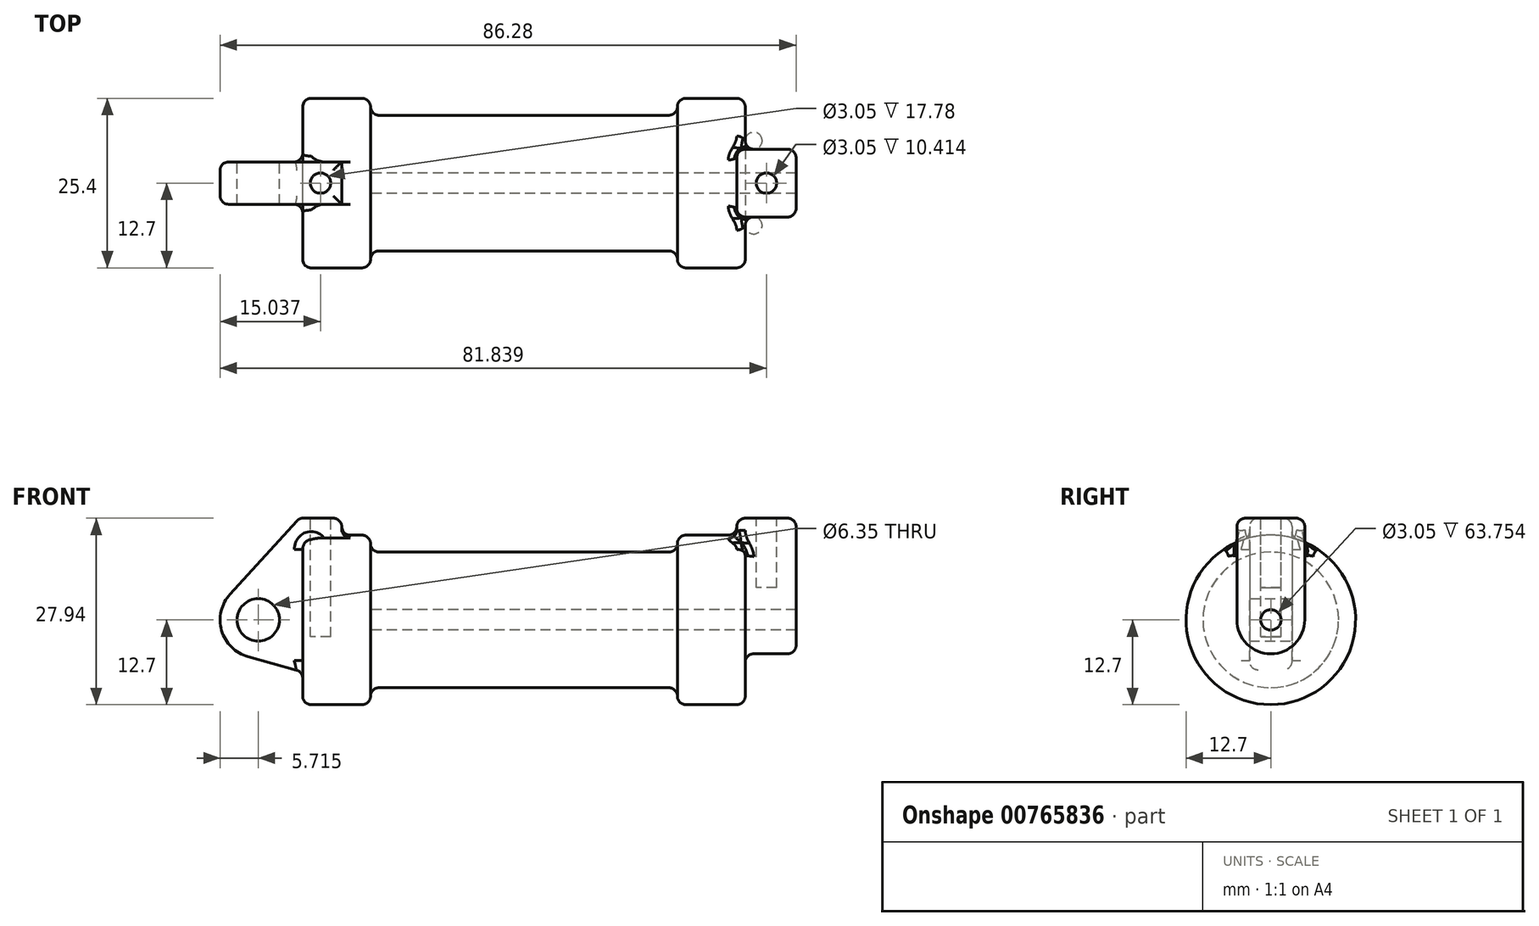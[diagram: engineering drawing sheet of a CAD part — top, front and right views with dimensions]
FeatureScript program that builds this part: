
annotation { "Feature Type Name" : "Feature", "Feature Type Description" : "" }
export const myFeature = defineFeature(function(context is Context, id is Id, definition is map)
    precondition{}
    {
        {
            var Q0;
            Q0=qCreatedBy(makeId("Front.planeOp"),FACE);
            var sketch = newSketch(context, id + "F0", { "sketchPlane" : qUnion([Q0])});
            skLineSegment(sketch, "E0", {"start": v(0, 0) * mm, "end": v(0, 12.7) * mm});
            skLineSegment(sketch, "E1", {"start": v(0, 12.7) * mm, "end": v(10.16, 12.7) * mm});
            skLineSegment(sketch, "E2", {"start": v(10.16, 12.7) * mm, "end": v(10.16, 10.16) * mm});
            skLineSegment(sketch, "E3", {"start": v(10.16, 10.16) * mm, "end": v(56.13, 10.16) * mm});
            skLineSegment(sketch, "E4", {"start": v(56.13, 10.16) * mm, "end": v(56.13, 12.7) * mm});
            skLineSegment(sketch, "E5", {"start": v(56.13, 12.7) * mm, "end": v(66.3, 12.7) * mm});
            skLineSegment(sketch, "E6", {"start": v(66.3, 12.7) * mm, "end": v(66.3, 0) * mm});
            skLineSegment(sketch, "E7", {"start": v(66.3, 0) * mm, "end": v(0, 0) * mm});
            skLineSegment(sketch, "E8", {"start": v(5.84, 15.24) * mm, "end": v(-0.5, 15.24) * mm});
            skLineSegment(sketch, "E9", {"start": v(-0.5, 15.24) * mm, "end": v(-10.88, 3.85) * mm});
            skLineSegment(sketch, "E10", {"start": v(0, 0) * mm, "end": v(-6.65, 0) * mm});
            skCircle(sketch, "E11", {"center": v(-6.65, 0) * mm, "radius": 5.72 * mm});
            skCircle(sketch, "E12", {"center": v(-6.65, 0) * mm, "radius": 3.18 * mm});
            skLineSegment(sketch, "E13", {"start": v(5.84, 15.24) * mm, "end": v(5.84, -9.4) * mm});
            skLineSegment(sketch, "E14", {"start": v(5.84, -9.4) * mm, "end": v(-8.18, -5.5) * mm});
            skSolve(sketch);
        }
        {
            var Q0;
            {var subQ0=sQuery(id+"F0.wireOp",EDGE,"E2");Q0=makeQuery(id+"F0.imprint","IMPRINT",FACE,{"disambiguationData":[TD([[makeQuery(id+"F0.imprint","IMPRINT",EDGE,{"derivedFrom":subQ0}),-1.0]])]});}
            var Q1;
            {var subQ0=sQuery(id+"F0.wireOp",EDGE,"E0");Q1=makeQuery(id+"F0.imprint","IMPRINT",FACE,{"disambiguationData":[TD([[makeQuery(id+"F0.imprint","IMPRINT",EDGE,{"derivedFrom":subQ0}),-1.0]])]});}
            var Q2;
            Q2=sQuery(id+"F0.wireOp",EDGE,"E7");
            revolve(context, id + "F1", {"surfaceOperationType" : NewSurfaceOperationType.NEW, "entities" : qUnion([Q0, Q1]), "axis" : qUnion([Q2]), "revolveType" : RevolveType.FULL});
        }
        {
            var Q0;
            {var subQ1=sQuery(id+"F0.wireOp",EDGE,"E0");Q0=makeQuery(id+"F0.imprint","IMPRINT",FACE,{"disambiguationData":[TD([[makeQuery(id+"F0.imprint","IMPRINT",EDGE,{"derivedFrom":subQ1}),1.0]])]});}
            var Q1;
            {var subQ5=sQuery(id+"F0.wireOp",EDGE,"E12");Q1=makeQuery(id+"F0.imprint","IMPRINT",FACE,{"disambiguationData":[TD([[makeQuery(id+"F0.imprint","IMPRINT",EDGE,{"derivedFrom":subQ5}),-1.0]])]});}
            var Q2;
            {var subQ0=sQuery(id+"F0.wireOp",EDGE,"E14");Q2=makeQuery(id+"F0.imprint","IMPRINT",FACE,{"disambiguationData":[TD([[makeQuery(id+"F0.imprint","IMPRINT",EDGE,{"derivedFrom":subQ0}),-1.0]])]});}
            var Q3;
            {var subQ0=sQuery(id+"F0.wireOp",EDGE,"E0");Q3=makeQuery(id+"F0.imprint","IMPRINT",FACE,{"disambiguationData":[TD([[makeQuery(id+"F0.imprint","IMPRINT",EDGE,{"derivedFrom":subQ0}),-1.0]])]});}
            extrude(context, id + "F2", {"entities" : qUnion([Q0, Q1, Q2, Q3]), "operationType" : NewBodyOperationType.ADD, "endBound" : BoundingType.SYMMETRIC, "depth" : 6.35 * mm, "offsetDistance" : 25.4 * mm});
        }
        {
            var Q0;
            Q0=makeQuery(id+"F1.opRevolve","SWEPT_FACE",FACE,{"disambiguationData":[OSD([sQuery(id+"F0.wireOp",EDGE,"E6")])]});
            var sketch = newSketch(context, id + "F3", { "sketchPlane" : qUnion([Q0])});
            skCircle(sketch, "E15", {"center": v(0, 0) * mm, "radius": 1.52 * mm});
            skCircle(sketch, "E16", {"center": v(0, 0) * mm, "radius": 5.08 * mm});
            skLineSegment(sketch, "E17", {"start": v(-5.08, 0) * mm, "end": v(-5.08, 15.24) * mm});
            skLineSegment(sketch, "E18", {"start": v(5.08, 0) * mm, "end": v(5.08, 15.24) * mm});
            skLineSegment(sketch, "E19", {"start": v(5.08, 15.24) * mm, "end": v(-5.08, 15.24) * mm});
            skSolve(sketch);
        }
        {
            var Q0;
            {var subQ0=sQuery(id+"F3.wireOp",EDGE,"E19");Q0=makeQuery(id+"F3.imprint","IMPRINT",FACE,{"disambiguationData":[TD([[makeQuery(id+"F3.imprint","IMPRINT",EDGE,{"derivedFrom":subQ0}),1.0]])]});}
            var Q1;
            {var subQ0=sQuery(id+"F3.wireOp",EDGE,"E17");var subQ1=sQuery(id+"F3.wireOp",EDGE,"E16");var subQ2=makeQuery(id+"F3.imprint","INTERSECT",VERTEX,{"derivedFrom":[subQ1,subQ0]});Q1=makeQuery(id+"F3.imprint","IMPRINT",FACE,{"disambiguationData":[TD([[makeQuery(id+"F3.imprint","IMPRINT",EDGE,{"disambiguationData":[TD([[subQ2,1.0]])],"derivedFrom":subQ1}),-1.0]])]});}
            var Q2;
            Q2=makeQuery(id+"F3.imprint","IMPRINT",FACE,{"disambiguationData":[TD([[makeQuery(id+"F3.imprint","IMPRINT",EDGE,{"derivedFrom":sQuery(id+"F3.wireOp",EDGE,"E15")}),-1.0]])]});
            extrude(context, id + "F4", {"entities" : qUnion([Q0, Q1, Q2]), "operationType" : NewBodyOperationType.ADD, "depth" : 7.62 * mm, "offsetDistance" : 25.4 * mm, "hasSecondDirection" : true, "secondDirectionOppositeDirection" : true, "secondDirectionDepth" : 1.27 * mm});
        }
        {
            var Q0;
            Q0=makeQuery(id+"F4.boolean.opBoolean","SPLIT",FACE,{"disambiguationData":[TD([makeQuery(id+"F4.opExtrude","SWEPT_FACE",FACE,{"disambiguationData":[OSD([sQuery(id+"F3.wireOp",EDGE,"E15")])]})])],"derivedFrom":makeQuery(id+"F1.opRevolve","SWEPT_FACE",FACE,{"disambiguationData":[OSD([sQuery(id+"F0.wireOp",EDGE,"E6")])]})});
            var Q1;
            Q1=makeQuery(id+"F1.opRevolve","SWEPT_FACE",FACE,{"disambiguationData":[OSD([sQuery(id+"F0.wireOp",EDGE,"E2")])]});
            extrude(context, id + "F5", {"entities" : qUnion([Q0]), "operationType" : NewBodyOperationType.REMOVE, "endBound" : BoundingType.UP_TO_SURFACE, "oppositeDirection" : true, "depth" : 25.4 * mm, "endBoundEntityFace" : qUnion([Q1]), "offsetDistance" : 25.4 * mm});
        }
        {
            var Q0;
            Q0=makeQuery(id+"F2.opExtrude","SWEPT_FACE",FACE,{"disambiguationData":[OSD([sQuery(id+"F0.wireOp",EDGE,"E8")])]});
            var sketch = newSketch(context, id + "F6", { "sketchPlane" : qUnion([Q0])});
            skCircle(sketch, "E20", {"center": v(2.67, 0) * mm, "radius": 1.52 * mm});
            skPoint(sketch, "E20.centerSnap0", {"position": v(-0.5, 0) * mm});
            skPoint(sketch, "E20.centerSnap1", {"position": v(2.67, 3.18) * mm});
            skSolve(sketch);
        }
        {
            var Q0;
            Q0=makeQuery(id+"F6.imprint","IMPRINT",FACE,{"disambiguationData":[TD([[makeQuery(id+"F6.imprint","IMPRINT",EDGE,{"derivedFrom":sQuery(id+"F6.wireOp",EDGE,"E20")}),1.0]])]});
            extrude(context, id + "F7", {"entities" : qUnion([Q0]), "operationType" : NewBodyOperationType.REMOVE, "oppositeDirection" : true, "depth" : 17.78 * mm, "offsetDistance" : 25.4 * mm});
        }
        {
            var Q0;
            Q0=makeQuery(id+"F4.opExtrude","SWEPT_FACE",FACE,{"disambiguationData":[OSD([sQuery(id+"F3.wireOp",EDGE,"E19")])]});
            var sketch = newSketch(context, id + "F8", { "sketchPlane" : qUnion([Q0])});
            skCircle(sketch, "E21", {"center": v(69.47, 0) * mm, "radius": 1.52 * mm});
            skPoint(sketch, "E21.centerSnap0", {"position": v(65.02, 0) * mm});
            skPoint(sketch, "E21.centerSnap1", {"position": v(69.47, -5.08) * mm});
            skSolve(sketch);
        }
        {
            var Q0;
            Q0=makeQuery(id+"F8.imprint","IMPRINT",FACE,{"disambiguationData":[TD([[makeQuery(id+"F8.imprint","IMPRINT",EDGE,{"derivedFrom":sQuery(id+"F8.wireOp",EDGE,"E21")}),1.0]])]});
            extrude(context, id + "F9", {"entities" : qUnion([Q0]), "operationType" : NewBodyOperationType.REMOVE, "oppositeDirection" : true, "depth" : 10.4 * mm, "offsetDistance" : 25.4 * mm});
        }
        {
            var Q0;
            Q0=makeQuery(id+"F1.opRevolve","SWEPT_EDGE",EDGE,{"disambiguationData":[OSD([sQuery(id+"F0.wireOp",EDGE,"E4"),sQuery(id+"F0.wireOp",EDGE,"E5")])]});
            var Q1;
            Q1=makeQuery(id+"F1.opRevolve","SWEPT_EDGE",EDGE,{"disambiguationData":[OSD([sQuery(id+"F0.wireOp",EDGE,"E3"),sQuery(id+"F0.wireOp",EDGE,"E4")])]});
            var Q2;
            Q2=makeQuery(id+"F1.opRevolve","SWEPT_EDGE",EDGE,{"disambiguationData":[OSD([sQuery(id+"F0.wireOp",EDGE,"E2"),sQuery(id+"F0.wireOp",EDGE,"E3")])]});
            var Q3;
            Q3=makeQuery(id+"F1.opRevolve","SWEPT_FACE",FACE,{"disambiguationData":[OSD([sQuery(id+"F0.wireOp",EDGE,"E2")])]});
            fillet(context, id + "F10", {"entities" : qUnion([Q0, Q1, Q2, Q3]), "radius" : 1.27 * mm, "tangentPropagation" : true, "allowEdgeOverflow" : false});
        }
        {
            var Q0;
            Q0=makeQuery(id+"F1.opRevolve","SWEPT_FACE",FACE,{"disambiguationData":[OSD([sQuery(id+"F0.wireOp",EDGE,"E0")])]});
            var Q1;
            Q1=makeQuery(id+"F2.boolean.opBoolean","INTERSECT",EDGE,{"derivedFrom":[makeQuery(id+"F1.opRevolve","SWEPT_FACE",FACE,{"disambiguationData":[OSD([sQuery(id+"F0.wireOp",EDGE,"E1")])]}),makeQuery(id+"F2.opExtrude","SWEPT_FACE",FACE,{"disambiguationData":[OSD([sQuery(id+"F0.wireOp",EDGE,"E13")])]})]});
            var Q2;
            Q2=makeQuery(id+"F2.opExtrude","CAP_EDGE",EDGE,{"disambiguationData":[OSD([sQuery(id+"F0.wireOp",EDGE,"E8")])],"isStart":false});
            var Q3;
            Q3=makeQuery(id+"F2.opExtrude","SWEPT_EDGE",EDGE,{"disambiguationData":[OSD([sQuery(id+"F0.wireOp",EDGE,"E8"),sQuery(id+"F0.wireOp",EDGE,"E9")])]});
            var Q4;
            Q4=makeQuery(id+"F2.opExtrude","CAP_EDGE",EDGE,{"disambiguationData":[OSD([sQuery(id+"F0.wireOp",EDGE,"E8")])],"isStart":true});
            var Q5;
            Q5=makeQuery(id+"F2.opExtrude","SWEPT_EDGE",EDGE,{"disambiguationData":[OSD([sQuery(id+"F0.wireOp",EDGE,"E8"),sQuery(id+"F0.wireOp",EDGE,"E13")])]});
            var Q6;
            Q6=makeQuery(id+"F2.opExtrude","SWEPT_FACE",FACE,{"disambiguationData":[OSD([sQuery(id+"F0.wireOp",EDGE,"E9")])]});
            fillet(context, id + "F11", {"entities" : qUnion([Q0, Q1, Q2, Q3, Q4, Q5, Q6]), "radius" : 1.27 * mm, "tangentPropagation" : true, "allowEdgeOverflow" : false});
        }
        {
            var Q0;
            Q0=makeQuery(id+"F4.boolean.opBoolean","SPLIT",FACE,{"disambiguationData":[TD([makeQuery(id+"F1.opRevolve","SWEPT_FACE",FACE,{"disambiguationData":[OSD([sQuery(id+"F0.wireOp",EDGE,"E5")])]})])],"derivedFrom":makeQuery(id+"F1.opRevolve","SWEPT_FACE",FACE,{"disambiguationData":[OSD([sQuery(id+"F0.wireOp",EDGE,"E6")])]})});
            var Q1;
            Q1=makeQuery(id+"F4.boolean.opBoolean","INTERSECT",EDGE,{"derivedFrom":[makeQuery(id+"F1.opRevolve","SWEPT_FACE",FACE,{"disambiguationData":[OSD([sQuery(id+"F0.wireOp",EDGE,"E5")])]}),makeQuery(id+"F4.opExtrude","CAP_FACE",FACE,{"disambiguationData":[OSD([sQuery(id+"F3.wireOp",EDGE,"E15"),sQuery(id+"F3.wireOp",EDGE,"E16"),sQuery(id+"F3.wireOp",EDGE,"E17"),sQuery(id+"F3.wireOp",EDGE,"E18"),sQuery(id+"F3.wireOp",EDGE,"E19")])],"isStart":true})]});
            var Q2;
            Q2=makeQuery(id+"F4.opExtrude","CAP_EDGE",EDGE,{"disambiguationData":[OSD([sQuery(id+"F3.wireOp",EDGE,"E18")])],"isStart":true});
            var Q3;
            Q3=makeQuery(id+"F1.opRevolve","SWEPT_EDGE",EDGE,{"disambiguationData":[OSD([sQuery(id+"F0.wireOp",EDGE,"E5"),sQuery(id+"F0.wireOp",EDGE,"E6")])]});
            var Q4;
            Q4=makeQuery(id+"F4.boolean.opBoolean","INTERSECT",EDGE,{"derivedFrom":[makeQuery(id+"F1.opRevolve","SWEPT_FACE",FACE,{"disambiguationData":[OSD([sQuery(id+"F0.wireOp",EDGE,"E5")])]}),makeQuery(id+"F4.opExtrude","SWEPT_FACE",FACE,{"disambiguationData":[OSD([sQuery(id+"F3.wireOp",EDGE,"E18")])]})]});
            var Q5;
            Q5=makeQuery(id+"F4.boolean.opBoolean","INTERSECT",EDGE,{"derivedFrom":[makeQuery(id+"F1.opRevolve","SWEPT_FACE",FACE,{"disambiguationData":[OSD([sQuery(id+"F0.wireOp",EDGE,"E5")])]}),makeQuery(id+"F4.opExtrude","SWEPT_FACE",FACE,{"disambiguationData":[OSD([sQuery(id+"F3.wireOp",EDGE,"E17")])]})]});
            var Q6;
            Q6=makeQuery(id+"F4.opExtrude","CAP_EDGE",EDGE,{"disambiguationData":[OSD([sQuery(id+"F3.wireOp",EDGE,"E17")])],"isStart":true});
            var Q7;
            Q7=makeQuery(id+"F4.opExtrude","CAP_FACE",FACE,{"disambiguationData":[OSD([sQuery(id+"F3.wireOp",EDGE,"E15"),sQuery(id+"F3.wireOp",EDGE,"E16"),sQuery(id+"F3.wireOp",EDGE,"E17"),sQuery(id+"F3.wireOp",EDGE,"E18"),sQuery(id+"F3.wireOp",EDGE,"E19")])],"isStart":true});
            var Q8;
            Q8=makeQuery(id+"F4.opExtrude","SWEPT_EDGE",EDGE,{"disambiguationData":[OSD([sQuery(id+"F3.wireOp",EDGE,"E17"),sQuery(id+"F3.wireOp",EDGE,"E19")])]});
            var Q9;
            Q9=makeQuery(id+"F4.opExtrude","SWEPT_FACE",FACE,{"disambiguationData":[OSD([sQuery(id+"F3.wireOp",EDGE,"E17")])]});
            var Q10;
            Q10=makeQuery(id+"F4.opExtrude","SWEPT_FACE",FACE,{"disambiguationData":[OSD([sQuery(id+"F3.wireOp",EDGE,"E16")])]});
            var Q11;
            Q11=makeQuery(id+"F4.opExtrude","SWEPT_FACE",FACE,{"disambiguationData":[OSD([sQuery(id+"F3.wireOp",EDGE,"E18")])]});
            var Q12;
            Q12=makeQuery(id+"F4.opExtrude","CAP_EDGE",EDGE,{"disambiguationData":[OSD([sQuery(id+"F3.wireOp",EDGE,"E19")])],"isStart":false});
            fillet(context, id + "F12", {"entities" : qUnion([Q0, Q1, Q2, Q3, Q4, Q5, Q6, Q7, Q8, Q9, Q10, Q11, Q12]), "radius" : 1.27 * mm, "tangentPropagation" : true, "allowEdgeOverflow" : false});
        }
    });
